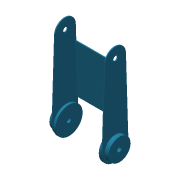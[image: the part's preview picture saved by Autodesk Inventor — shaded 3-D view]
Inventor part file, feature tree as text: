
AUTODESK INVENTOR PART (.ipt)
format: ipt  version: 2016 (Build 200138000, 138)  size: 153,088 bytes
history: native  units: in
note: dims shown in document units (in); Inventor stores cm internally (conversion verified against a paired STEP export)
features: extrude x7, sketch x7, plane x3, mirror x1, projected_geometry x1
ambient origin geometry x8: Origin, YZ Plane, XZ Plane, XY Plane, X Axis, Y Axis, Z Axis, Center Point
bodies: Solid1 (feature_tree)
feature tree (19):
  extrude  "Extrusion1"  Depth=0.45in TaperAngle=0.0deg
  extrude  "Extrusion2"  Depth=2.35in
  plane  "Work Plane1"
  extrude  "Extrusion4"  Depth=0.11in TaperAngle=0.0deg
  plane  "Work Plane2"
  extrude  "Extrusion5"  Depth=0.11in TaperAngle=0.0deg
  plane  "Work Plane3"
  mirror  "Mirror1"
  extrude  "Extrusion6"  Depth=0.16in
  extrude  "Extrusion3"  Depth=5.5625in
  extrude  "Extrusion7"  Depth=5.5625in
  sketch  "Sketch1"  dims[d0=2.5in d1=0.45in d2=0.0in]
  sketch  "Sketch2"  dims[d3=0.2in d4=2.35in]
  projected_geometry  "Projected Loop1"
  sketch  "Sketch3"  dims[d5=8.6875in d6=0.11in d7=0.0in]
  sketch  "Sketch4"  dims[d8=0.5in d9=0.11in d10=0.0in]
  sketch  "Sketch5"  dims[d11=0.16in d12=3.08in]
  sketch  "Sketch6"  dims[d13=0.25in d14=0.0in d15=5.5625in]
  sketch  "Sketch7"  dims[d16=0.11in d17=5.5625in d18=1.5in d19=0.25in d20=0.0in d21=2.7812in d22=0.25in d23=0.0in d24=0.5in d25=0.25in d26=0.0in]
